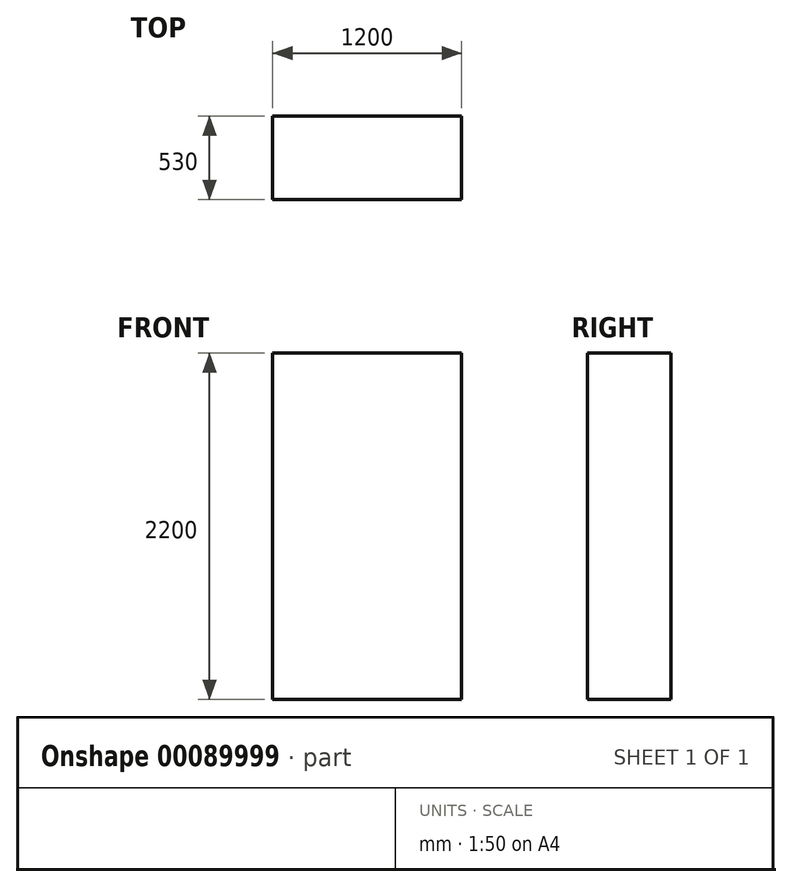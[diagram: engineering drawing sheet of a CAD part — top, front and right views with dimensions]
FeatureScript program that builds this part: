
annotation { "Feature Type Name" : "Feature", "Feature Type Description" : "" }
export const myFeature = defineFeature(function(context is Context, id is Id, definition is map)
    precondition{}
    {
        {
            var Q0;
            Q0=qCreatedBy(makeId("Top.planeOp"),FACE);
            var sketch = newSketch(context, id + "F0", { "sketchPlane" : qUnion([Q0])});
            skLineSegment(sketch, "E0.bottom", {"start": v(0, 0) * mm, "end": v(1200, 0) * mm});
            skLineSegment(sketch, "E0.top", {"start": v(0, 530) * mm, "end": v(1200, 530) * mm});
            skLineSegment(sketch, "E0.left", {"start": v(0, 0) * mm, "end": v(0, 530) * mm});
            skLineSegment(sketch, "E0.right", {"start": v(1200, 0) * mm, "end": v(1200, 530) * mm});
            skSolve(sketch);
        }
        {
            var Q0;
            Q0 = qSketchRegion(id + "F0", true);
            extrude(context, id + "F1", {"entities" : qUnion([Q0]), "depth" : 2200 * mm});
        }
    });
